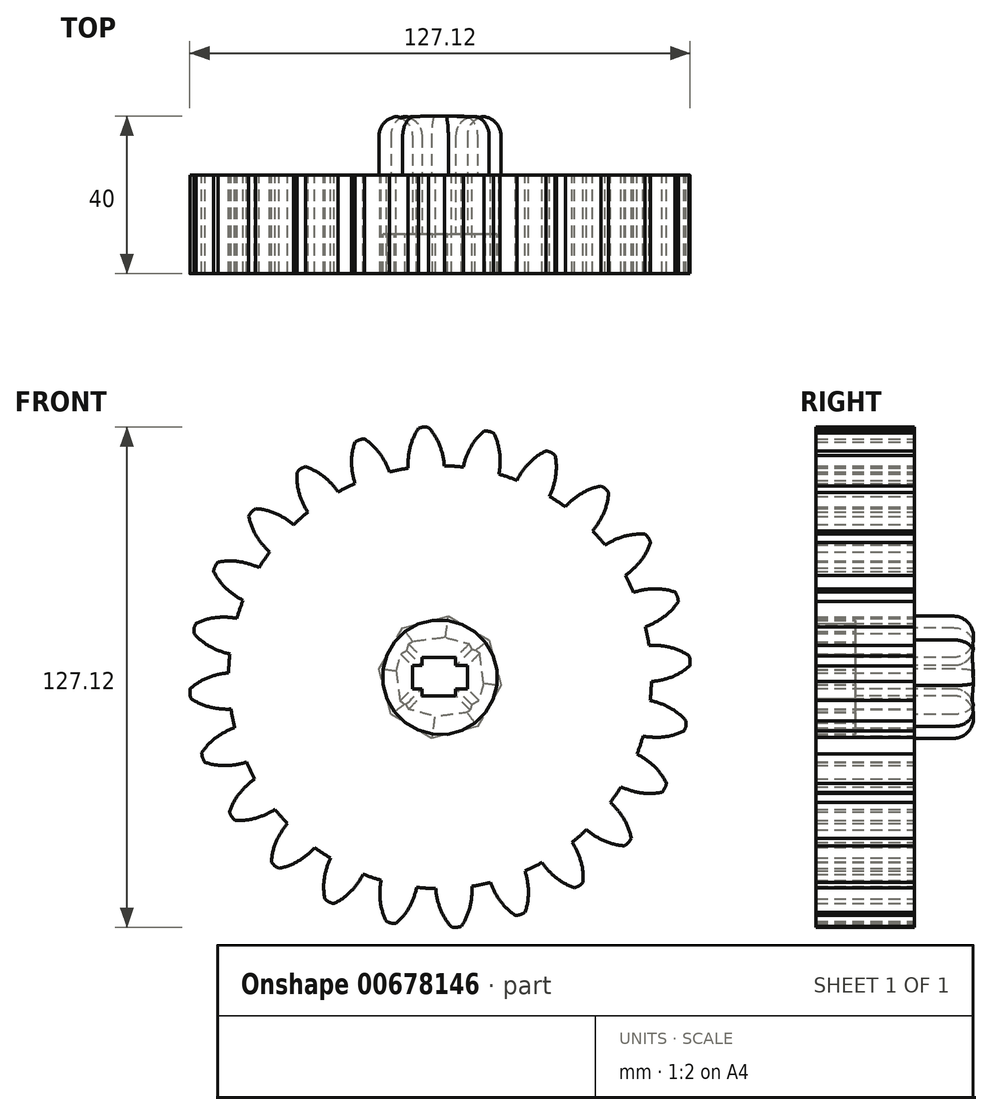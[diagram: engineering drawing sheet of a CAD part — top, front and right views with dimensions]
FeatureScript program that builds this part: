
annotation { "Feature Type Name" : "Feature", "Feature Type Description" : "" }
export const myFeature = defineFeature(function(context is Context, id is Id, definition is map)
    precondition{}
    {
        {
            var Q0;
            Q0=qCreatedBy(makeId("Front.planeOp"),FACE);
            var sketch = newSketch(context, id + "F0", { "sketchPlane" : qUnion([Q0])});
            skCircle(sketch, "E0", {"center": v(0, 0) * mm, "radius": 53.72 * mm});
            skCircle(sketch, "E1", {"center": v(0, 0) * mm, "radius": 58.67 * mm, "construction": true});
            skCircle(sketch, "E2", {"center": v(0, 0) * mm, "radius": 63.5 * mm, "construction": true});
            skLineSegment(sketch, "E3", {"start": v(0, 0) * mm, "end": v(0, 91.84) * mm, "construction": true});
            skLineSegment(sketch, "E4", {"start": v(0, 0) * mm, "end": v(-7.41, 113.09) * mm, "construction": true});
            skLineSegment(sketch, "E5", {"start": v(0, 58.67) * mm, "end": v(-83.5, 56.59) * mm, "construction": true});
            skLineSegment(sketch, "E6", {"start": v(0, 58.67) * mm, "end": v(-75.39, 29.08) * mm, "construction": true});
            skCircle(sketch, "E7", {"center": v(0, 0) * mm, "radius": 54.62 * mm, "construction": true});
            skCircle(sketch, "E8", {"center": v(0, 58.67) * mm, "radius": 16.52 * mm, "construction": true});
            skCircle(sketch, "E9", {"center": v(-15.38, 52.64) * mm, "radius": 16.52 * mm, "construction": true});
            skArc(sketch, "E10", {"start": v(0, 58.67) * mm, "mid": v(-1.21, 61.19) * mm, "end": v(-2.87, 63.43) * mm});
            skArc(sketch, "E11", {"start": v(1.1, 53.7) * mm, "mid": v(0.72, 56.23) * mm, "end": v(0, 58.67) * mm});
            skArc(sketch, "E12.MirrorCS", {"start": v(-8.1, 53.1) * mm, "mid": v(-8.06, 55.65) * mm, "end": v(-7.66, 58.17) * mm});
            skArc(sketch, "E13.MirrorCS", {"start": v(-7.66, 58.17) * mm, "mid": v(-6.78, 60.82) * mm, "end": v(-5.43, 63.27) * mm});
            skArc(sketch, "E14", {"start": v(-2.87, 63.43) * mm, "mid": v(-4.17, 63.55) * mm, "end": v(-5.43, 63.27) * mm});
            skCircle(sketch, "E15.cCircle", {"center": v(0, 0) * mm, "radius": 14.46 * mm, "construction": true});
            skLineSegment(sketch, "E15.0", {"start": v(-15.51, 2.1) * mm, "end": v(-9.48, 12.46) * mm});
            skLineSegment(sketch, "E15.1", {"start": v(-9.48, 12.46) * mm, "end": v(2.1, 15.51) * mm});
            skLineSegment(sketch, "E15.2", {"start": v(2.1, 15.51) * mm, "end": v(12.46, 9.48) * mm});
            skLineSegment(sketch, "E15.3", {"start": v(12.46, 9.48) * mm, "end": v(15.51, -2.1) * mm});
            skLineSegment(sketch, "E15.4", {"start": v(15.51, -2.1) * mm, "end": v(9.48, -12.46) * mm});
            skLineSegment(sketch, "E15.5", {"start": v(9.48, -12.46) * mm, "end": v(-2.1, -15.51) * mm});
            skLineSegment(sketch, "E15.6", {"start": v(-2.1, -15.51) * mm, "end": v(-12.46, -9.48) * mm});
            skLineSegment(sketch, "E15.7", {"start": v(-12.46, -9.48) * mm, "end": v(-15.51, 2.1) * mm});
            skPoint(sketch, "E15.0.midPoint", {"position": v(-12.5, 7.28) * mm});
            skLineSegment(sketch, "E16.bottom", {"start": v(-4.6, 5.04) * mm, "end": v(4, 5.04) * mm});
            skLineSegment(sketch, "E16.top", {"start": v(-4.6, -4.7) * mm, "end": v(4, -4.7) * mm});
            skLineSegment(sketch, "E16.left", {"start": v(-4.6, 5.04) * mm, "end": v(-4.6, -4.7) * mm});
            skLineSegment(sketch, "E16.right", {"start": v(4, 5.04) * mm, "end": v(4, -4.7) * mm});
            skLineSegment(sketch, "E17.bottom", {"start": v(-7.04, 2.93) * mm, "end": v(6.93, 2.93) * mm});
            skLineSegment(sketch, "E17.top", {"start": v(-7.04, -2.92) * mm, "end": v(6.93, -2.92) * mm});
            skLineSegment(sketch, "E17.left", {"start": v(-7.04, 2.93) * mm, "end": v(-7.04, -2.92) * mm});
            skLineSegment(sketch, "E17.right", {"start": v(6.93, 2.93) * mm, "end": v(6.93, -2.92) * mm});
            skSolve(sketch);
        }
        {
            var Q0;
            {var subQ0=sQuery(id+"F0.wireOp",EDGE,"E0");var subQ1=makeQuery(id+"F0.imprint","INTERSECT",VERTEX,{"derivedFrom":[subQ0,sQuery(id+"F0.wireOp",EDGE,"E11")]});Q0=makeQuery(id+"F0.imprint","IMPRINT",FACE,{"disambiguationData":[TD([[makeQuery(id+"F0.imprint","IMPRINT",EDGE,{"disambiguationData":[TD([[subQ1,-1.0]])],"derivedFrom":subQ0}),1.0]])]});}
            var Q1;
            Q1=makeQuery(id+"F0.imprint","IMPRINT",FACE,{"disambiguationData":[TD([[makeQuery(id+"F0.imprint","IMPRINT",EDGE,{"derivedFrom":sQuery(id+"F0.wireOp",EDGE,"E10")}),1.0]])]});
            extrude(context, id + "F1", {"entities" : qUnion([Q0, Q1]), "depth" : 25 * mm, "offsetDistance" : 25 * mm});
        }
        {
            var Q0;
            Q0=makeQuery(id+"F1.opExtrude","SWEPT_BODY",BODY,{"disambiguationData":[OSD([sQuery(id+"F0.wireOp",EDGE,"E0"),sQuery(id+"F0.wireOp",EDGE,"E10"),sQuery(id+"F0.wireOp",EDGE,"E11"),sQuery(id+"F0.wireOp",EDGE,"E12.MirrorCS"),sQuery(id+"F0.wireOp",EDGE,"E13.MirrorCS"),sQuery(id+"F0.wireOp",EDGE,"E14")])]});
            var Q1;
            Q1=makeQuery(id+"F1.opExtrude","SWEPT_FACE",FACE,{"disambiguationData":[OSD([sQuery(id+"F0.wireOp",EDGE,"E0")])]});
            circularPattern(context, id + "F2", {"entities" : qUnion([Q0]), "axis" : qUnion([Q1]), "angle" : 360 * degree, "instanceCount" : 24, "equalSpace" : true});
        }
        {
            var Q0;
            Q0=makeQuery(id+"F0.imprint","IMPRINT",FACE,{"disambiguationData":[TD([[makeQuery(id+"F0.imprint","IMPRINT",EDGE,{"derivedFrom":sQuery(id+"F0.wireOp",EDGE,"E15.0")}),-1.0]])]});
            extrude(context, id + "F3", {"entities" : qUnion([Q0]), "operationType" : NewBodyOperationType.ADD, "endBound" : BoundingType.SYMMETRIC, "oppositeDirection" : true, "depth" : 30 * mm, "offsetDistance" : 25 * mm});
        }
        {
            var Q0;
            Q0=makeQuery(id+"F3.opExtrude","CAP_FACE",FACE,{"disambiguationData":[OSD([sQuery(id+"F0.wireOp",EDGE,"E15.0"),sQuery(id+"F0.wireOp",EDGE,"E15.1"),sQuery(id+"F0.wireOp",EDGE,"E15.2"),sQuery(id+"F0.wireOp",EDGE,"E15.3"),sQuery(id+"F0.wireOp",EDGE,"E15.4"),sQuery(id+"F0.wireOp",EDGE,"E15.5"),sQuery(id+"F0.wireOp",EDGE,"E15.6"),sQuery(id+"F0.wireOp",EDGE,"E15.7"),sQuery(id+"F0.wireOp",EDGE,"E16.bottom"),sQuery(id+"F0.wireOp",EDGE,"E16.top"),sQuery(id+"F0.wireOp",EDGE,"E16.left"),sQuery(id+"F0.wireOp",EDGE,"E16.right"),sQuery(id+"F0.wireOp",EDGE,"E17.bottom"),sQuery(id+"F0.wireOp",EDGE,"E17.top"),sQuery(id+"F0.wireOp",EDGE,"E17.left"),sQuery(id+"F0.wireOp",EDGE,"E17.right")])],"isStart":false});
            fillet(context, id + "F4", {"entities" : qUnion([Q0]), "radius" : 5 * mm, "tangentPropagation" : true, "allowEdgeOverflow" : false});
        }
    });
